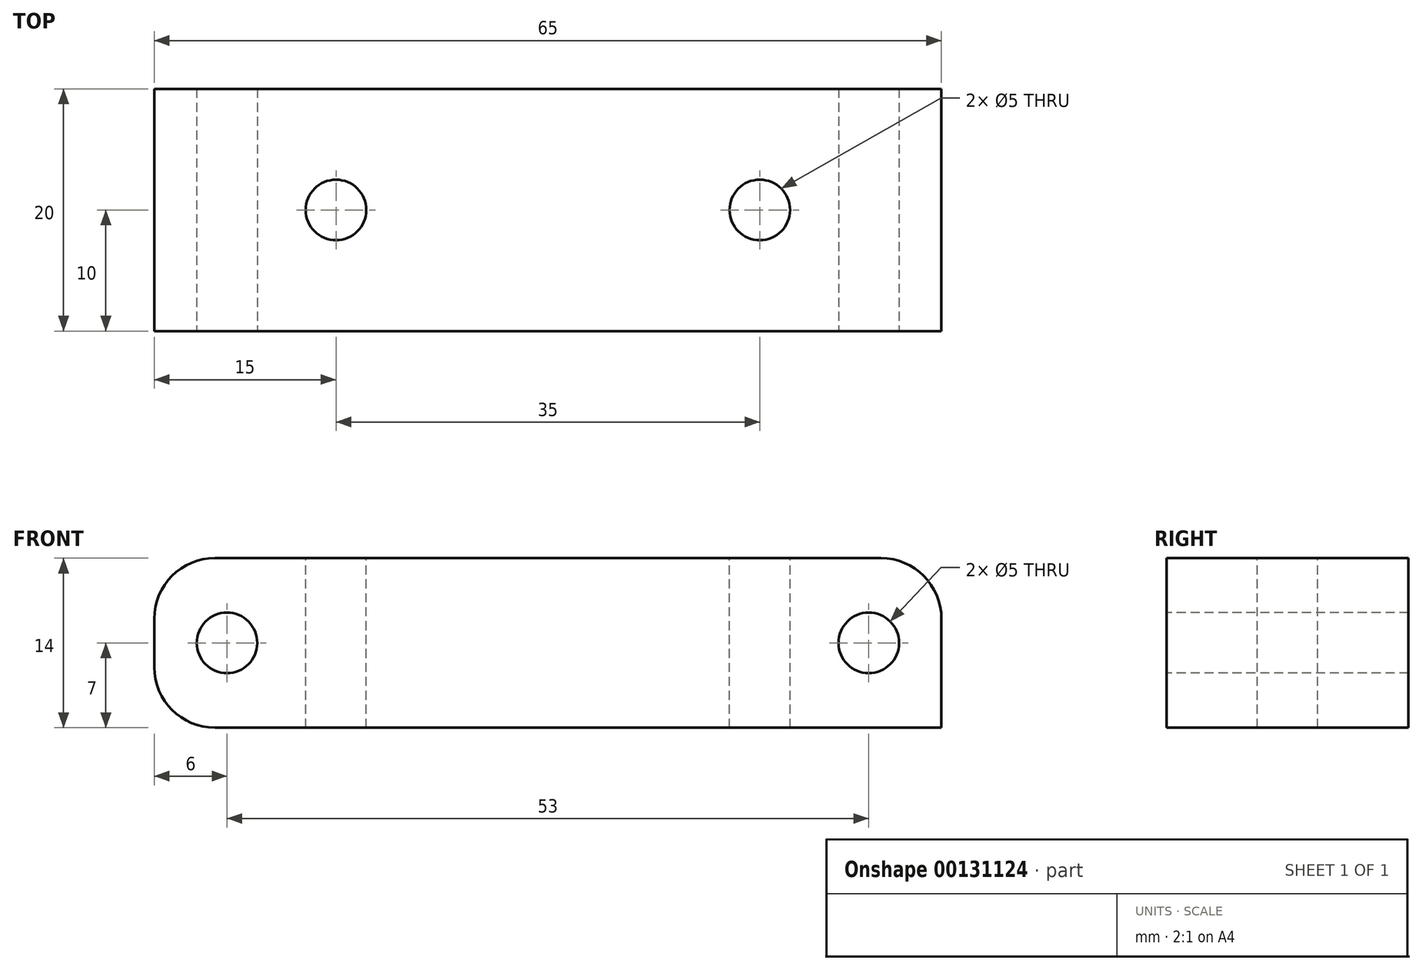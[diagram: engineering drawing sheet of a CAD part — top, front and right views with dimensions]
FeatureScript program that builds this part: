
annotation { "Feature Type Name" : "Feature", "Feature Type Description" : "" }
export const myFeature = defineFeature(function(context is Context, id is Id, definition is map)
    precondition{}
    {
        {
            var Q0;
            Q0=qCreatedBy(makeId("Right.planeOp"),FACE);
            var sketch = newSketch(context, id + "F0", { "sketchPlane" : qUnion([Q0])});
            skLineSegment(sketch, "E0.bottom", {"start": v(10, -7) * mm, "end": v(-10, -7) * mm});
            skLineSegment(sketch, "E0.top", {"start": v(10, 7) * mm, "end": v(-10, 7) * mm});
            skLineSegment(sketch, "E0.left", {"start": v(10, -7) * mm, "end": v(10, 7) * mm});
            skLineSegment(sketch, "E0.right", {"start": v(-10, -7) * mm, "end": v(-10, 7) * mm});
            skPoint(sketch, "E0.middle", {"position": v(0, 0) * mm});
            skSolve(sketch);
        }
        {
            var Q0;
            Q0=makeQuery(id+"F0.imprint","IMPRINT",FACE,{"disambiguationData":[TD([[makeQuery(id+"F0.imprint","IMPRINT",EDGE,{"derivedFrom":sQuery(id+"F0.wireOp",EDGE,"E0.bottom")}),-1.0]])]});
            extrude(context, id + "F1", {"entities" : qUnion([Q0]), "endBound" : BoundingType.SYMMETRIC, "depth" : 65 * mm});
        }
        {
            var Q0;
            Q0=makeQuery(id+"F1.opExtrude","SWEPT_FACE",FACE,{"disambiguationData":[OSD([sQuery(id+"F0.wireOp",EDGE,"E0.right")])]});
            var sketch = newSketch(context, id + "F2", { "sketchPlane" : qUnion([Q0])});
            skPoint(sketch, "E1", {"position": v(-26.5, 0) * mm});
            skPoint(sketch, "E2", {"position": v(26.5, 0) * mm});
            skSolve(sketch);
        }
        {
            var Q0;
            Q0=sQuery(id+"F2.wireOp",VERTEX,"E1");
            var Q1;
            Q1=sQuery(id+"F2.wireOp",VERTEX,"E2");
            var Q2;
            Q2=makeQuery(id+"F1.opExtrude","SWEPT_BODY",BODY,{"disambiguationData":[OSD([sQuery(id+"F0.wireOp",EDGE,"E0.bottom"),sQuery(id+"F0.wireOp",EDGE,"E0.top"),sQuery(id+"F0.wireOp",EDGE,"E0.left"),sQuery(id+"F0.wireOp",EDGE,"E0.right")])]});
            hole(context, id + "F3", {"style" : HoleStyle.SIMPLE, "endStyle" : HoleEndStyle.THROUGH, "standardTappedOrClearance" : lookupTablePath({ "standard" : "Custom", "fit" : "Normal", "size" : "M6", "type" : "Clearance" }), "standardBlindInLast" : lookupTablePath({ "fit" : "Standard", "standard" : "Custom", "size" : "M6", "type" : "Clearance" }), "holeDiameter" : 5 * mm, "locations" : qUnion([Q0, Q1]), "scope" : qUnion([Q2]), "isTappedThrough" : true});
        }
        {
            var Q0;
            Q0=makeQuery(id+"F1.opExtrude","SWEPT_FACE",FACE,{"disambiguationData":[OSD([sQuery(id+"F0.wireOp",EDGE,"E0.top")])]});
            var sketch = newSketch(context, id + "F4", { "sketchPlane" : qUnion([Q0])});
            skPoint(sketch, "E3", {"position": v(-17.5, 0) * mm});
            skPoint(sketch, "E3.positionSnap0", {"position": v(-32.5, 0) * mm});
            skPoint(sketch, "E4", {"position": v(17.5, 0) * mm});
            skSolve(sketch);
        }
        {
            var Q0;
            Q0=sQuery(id+"F4.wireOp",VERTEX,"E3");
            var Q1;
            Q1=sQuery(id+"F4.wireOp",VERTEX,"E4");
            var Q2;
            Q2=makeQuery(id+"F1.opExtrude","SWEPT_BODY",BODY,{"disambiguationData":[OSD([sQuery(id+"F0.wireOp",EDGE,"E0.bottom"),sQuery(id+"F0.wireOp",EDGE,"E0.top"),sQuery(id+"F0.wireOp",EDGE,"E0.left"),sQuery(id+"F0.wireOp",EDGE,"E0.right")])]});
            hole(context, id + "F5", {"style" : HoleStyle.SIMPLE, "endStyle" : HoleEndStyle.THROUGH, "holeDiameter" : 5 * mm, "locations" : qUnion([Q0, Q1]), "scope" : qUnion([Q2]), "isTappedThrough" : true});
        }
        {
            var Q0;
            Q0=makeQuery(id+"F1.opExtrude","CAP_EDGE",EDGE,{"disambiguationData":[OSD([sQuery(id+"F0.wireOp",EDGE,"E0.top")])],"isStart":false});
            var Q1;
            Q1=makeQuery(id+"F1.opExtrude","CAP_EDGE",EDGE,{"disambiguationData":[OSD([sQuery(id+"F0.wireOp",EDGE,"E0.bottom")])],"isStart":true});
            var Q2;
            Q2=makeQuery(id+"F1.opExtrude","CAP_EDGE",EDGE,{"disambiguationData":[OSD([sQuery(id+"F0.wireOp",EDGE,"E0.top")])],"isStart":true});
            fillet(context, id + "F6", {"entities" : qUnion([Q0, Q1, Q2]), "radius" : 5 * mm, "tangentPropagation" : true, "allowEdgeOverflow" : false});
        }
    });
